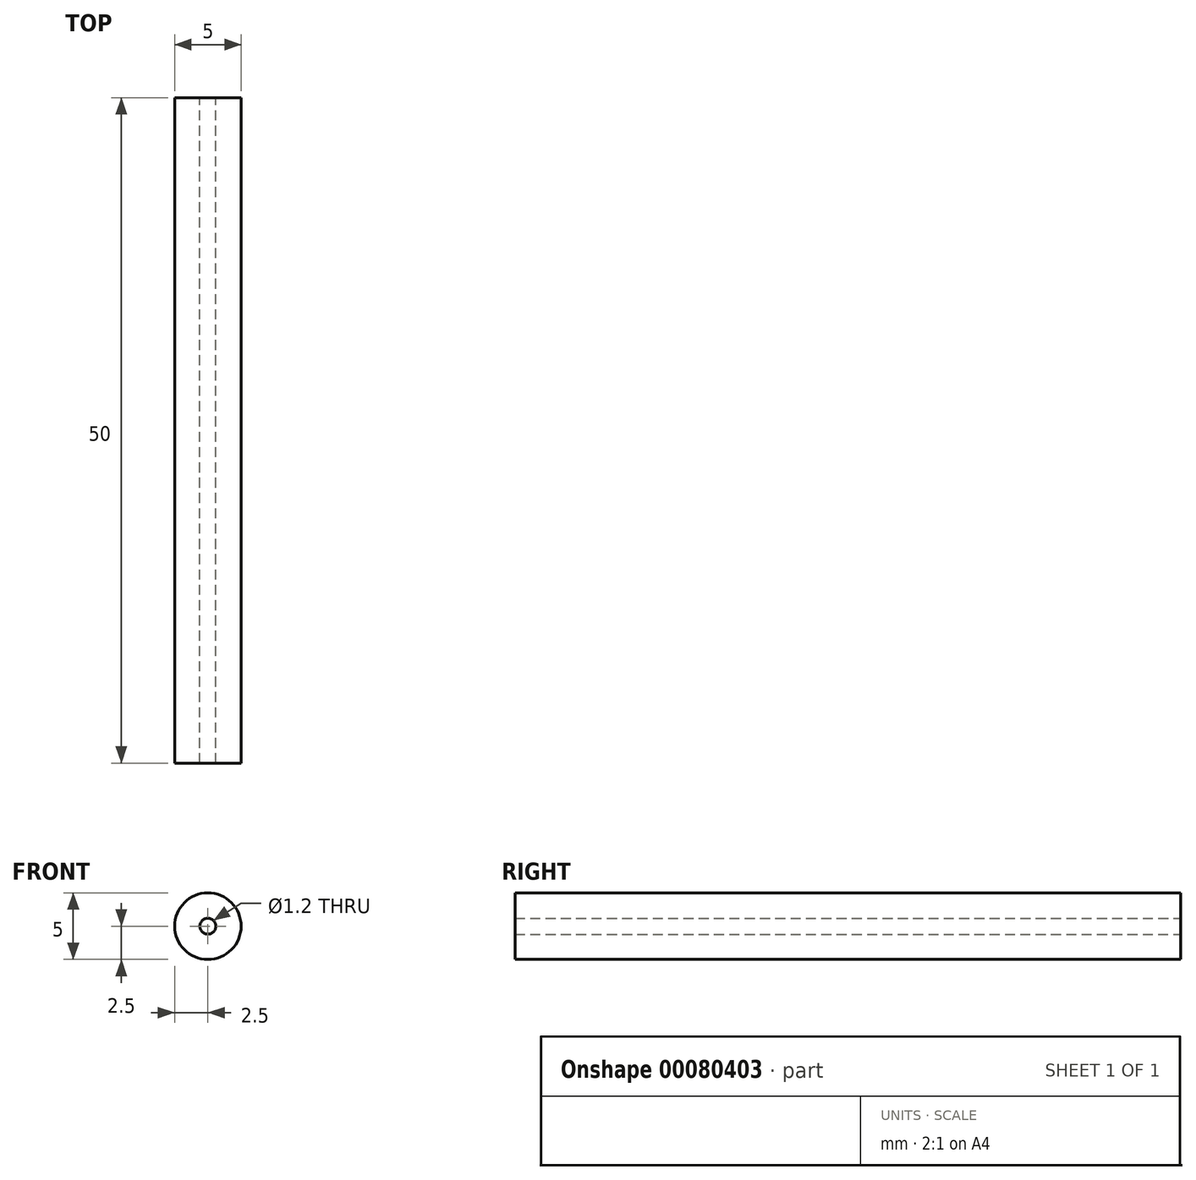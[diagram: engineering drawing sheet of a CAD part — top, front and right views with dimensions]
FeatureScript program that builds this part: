
annotation { "Feature Type Name" : "Feature", "Feature Type Description" : "" }
export const myFeature = defineFeature(function(context is Context, id is Id, definition is map)
    precondition{}
    {
        {
            var Q0;
            Q0=qCreatedBy(makeId("Front.planeOp"),FACE);
            var sketch = newSketch(context, id + "F0", { "sketchPlane" : qUnion([Q0])});
            skCircle(sketch, "E0", {"center": v(0, 0) * mm, "radius": 2.5 * mm});
            skSolve(sketch);
        }
        {
            var Q0;
            Q0=makeQuery(id+"F0.imprint","IMPRINT",FACE,{"disambiguationData":[TD([[makeQuery(id+"F0.imprint","IMPRINT",EDGE,{"derivedFrom":sQuery(id+"F0.wireOp",EDGE,"E0")}),1.0]])]});
            extrude(context, id + "F1", {"entities" : qUnion([Q0]), "depth" : 50 * mm});
        }
        {
            var Q0;
            Q0=makeQuery(id+"F1.opExtrude","CAP_FACE",FACE,{"disambiguationData":[OSD([sQuery(id+"F0.wireOp",EDGE,"E0")])],"isStart":true});
            var sketch = newSketch(context, id + "F2", { "sketchPlane" : qUnion([Q0])});
            skCircle(sketch, "E1", {"center": v(0, 0) * mm, "radius": 0.6 * mm});
            skSolve(sketch);
        }
        {
            var Q0;
            Q0=makeQuery(id+"F2.imprint","IMPRINT",FACE,{"disambiguationData":[TD([[makeQuery(id+"F2.imprint","IMPRINT",EDGE,{"derivedFrom":sQuery(id+"F2.wireOp",EDGE,"E1")}),1.0]])]});
            extrude(context, id + "F3", {"entities" : qUnion([Q0]), "operationType" : NewBodyOperationType.REMOVE, "oppositeDirection" : true, "depth" : 50 * mm});
        }
    });
